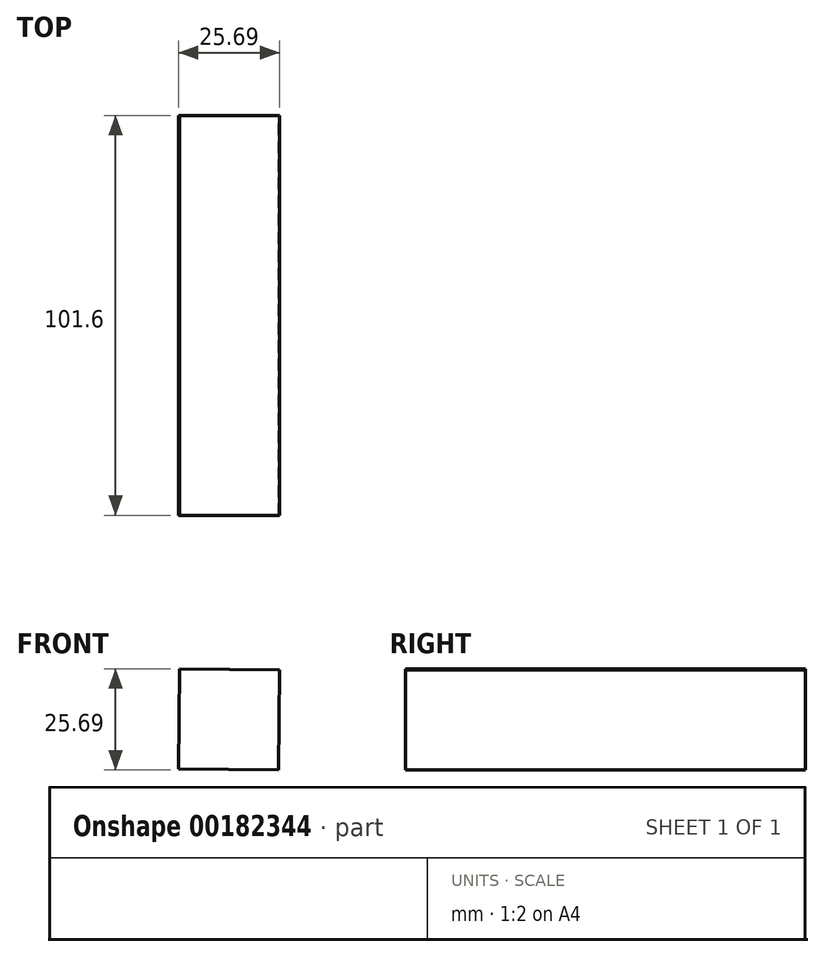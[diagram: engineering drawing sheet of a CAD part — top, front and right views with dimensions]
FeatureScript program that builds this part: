
annotation { "Feature Type Name" : "Feature", "Feature Type Description" : "" }
export const myFeature = defineFeature(function(context is Context, id is Id, definition is map)
    precondition{}
    {
        {
            var Q0;
            Q0=qCreatedBy(makeId("Front.planeOp"),FACE);
            var sketch = newSketch(context, id + "F0", { "sketchPlane" : qUnion([Q0])});
            skLineSegment(sketch, "E0", {"start": v(-18.52, 14.13) * mm, "end": v(-18.81, -11.26) * mm});
            skLineSegment(sketch, "E1", {"start": v(-18.81, -11.26) * mm, "end": v(6.58, -11.56) * mm});
            skLineSegment(sketch, "E2", {"start": v(6.58, -11.56) * mm, "end": v(6.88, 13.84) * mm});
            skLineSegment(sketch, "E3", {"start": v(6.88, 13.84) * mm, "end": v(-18.52, 14.13) * mm});
            skSolve(sketch);
        }
        {
            var Q0;
            Q0 = qSketchRegion(id + "F0", true);
            extrude(context, id + "F1", {"entities" : qUnion([Q0]), "depth" : 101.6 * mm});
        }
    });
